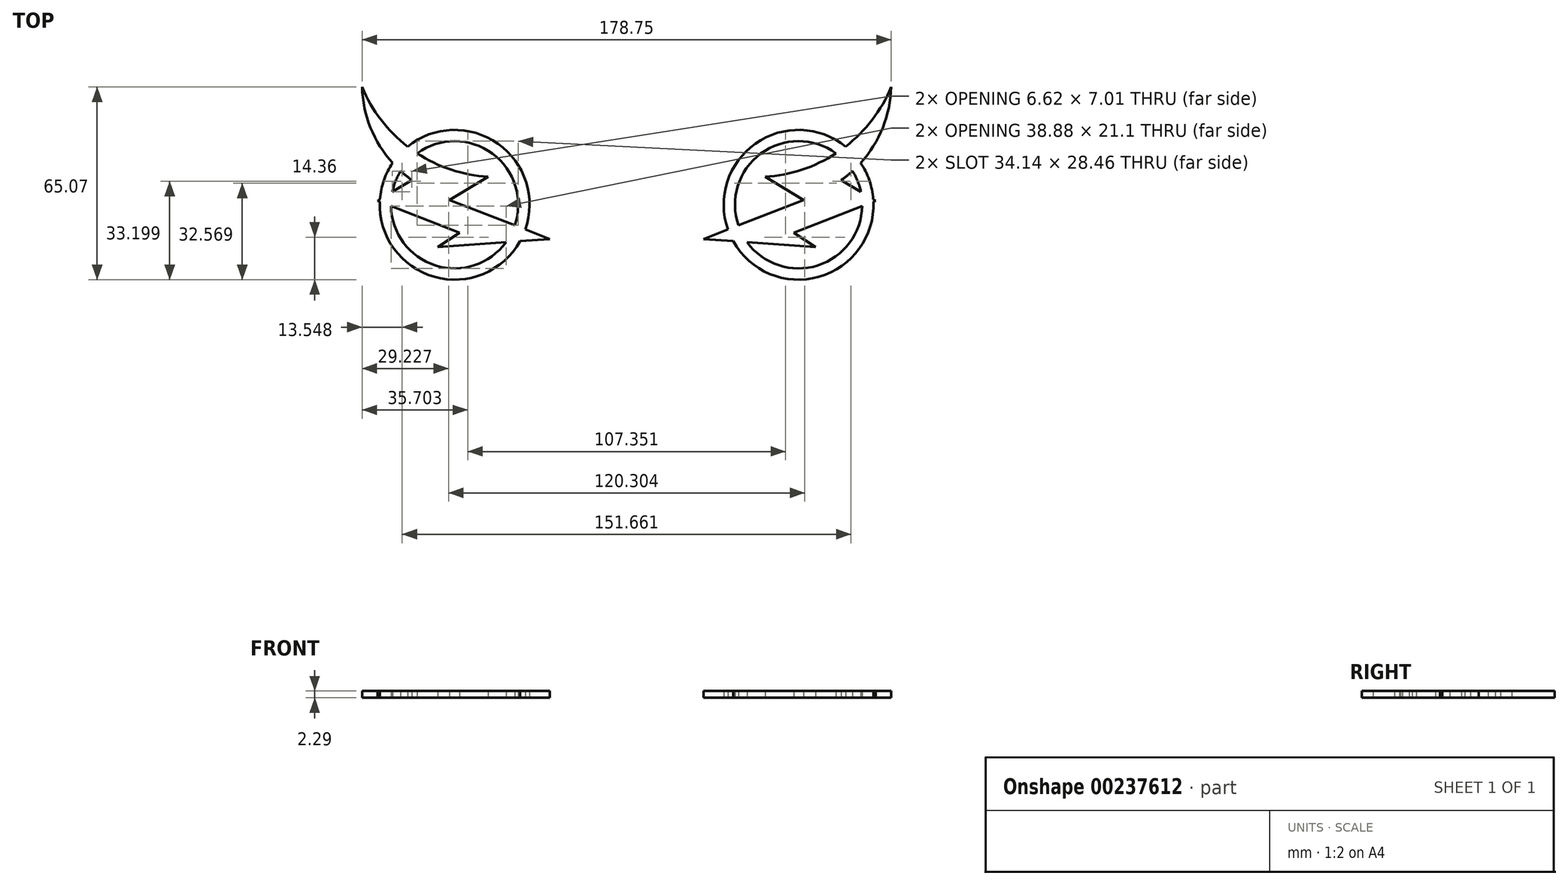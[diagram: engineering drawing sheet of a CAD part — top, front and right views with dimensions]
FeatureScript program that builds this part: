
annotation { "Feature Type Name" : "Feature", "Feature Type Description" : "" }
export const myFeature = defineFeature(function(context is Context, id is Id, definition is map)
    precondition{}
    {
        {
            var Q0;
            Q0=qCreatedBy(makeId("Top.planeOp"),FACE);
            var sketch = newSketch(context, id + "F0", { "sketchPlane" : qUnion([Q0])});
            skArc(sketch, "E0", {"start": v(-29.54, 23.2) * mm, "mid": v(-23.15, 12.16) * mm, "end": v(-14.15, 3.13) * mm});
            skLineSegment(sketch, "E1", {"start": v(13.05, -7.14) * mm, "end": v(0, -14.95) * mm});
            skLineSegment(sketch, "E2", {"start": v(0, -14.95) * mm, "end": v(22.07, -23.53) * mm});
            skLineSegment(sketch, "E3", {"start": v(33.89, -28.13) * mm, "end": v(23.86, -28.86) * mm});
            skLineSegment(sketch, "E4", {"start": v(-3.95, -30.88) * mm, "end": v(3.39, -25.96) * mm});
            skLineSegment(sketch, "E5", {"start": v(3.39, -25.96) * mm, "end": v(-19.75, -16.96) * mm});
            skLineSegment(sketch, "E6", {"start": v(-24.33, -15.18) * mm, "end": v(-23.5, -14.69) * mm});
            skArc(sketch, "E7", {"start": v(-29.54, 23.2) * mm, "mid": v(-26.67, 9.47) * mm, "end": v(-19.24, -2.41) * mm});
            skArc(sketch, "E8", {"start": v(-16.48, -5.17) * mm, "mid": v(-18.2, -8.55) * mm, "end": v(-19.3, -12.18) * mm});
            skArc(sketch, "E9.0", {"start": v(-19.24, -2.41) * mm, "mid": v(-22.17, -8.27) * mm, "end": v(-23.5, -14.69) * mm});
            skArc(sketch, "E10.trimOffspring", {"start": v(-10.9, 0.82) * mm, "mid": v(0.56, -4.71) * mm, "end": v(13.05, -7.14) * mm});
            skArc(sketch, "E11.trimOffspring", {"start": v(-16.48, -5.17) * mm, "mid": v(-14.63, -6.75) * mm, "end": v(-12.68, -8.21) * mm});
            skLineSegment(sketch, "E12.trimOffspring", {"start": v(-23.54, -15.49) * mm, "end": v(-24.33, -15.18) * mm});
            skLineSegment(sketch, "E13.trimOffspring", {"start": v(-19.3, -12.18) * mm, "end": v(-12.68, -8.21) * mm});
            skArc(sketch, "E14.trimOffspring", {"start": v(-19.75, -16.96) * mm, "mid": v(-4.72, -37.07) * mm, "end": v(19.12, -29.2) * mm});
            skArc(sketch, "E15.trimOffspring", {"start": v(-23.54, -15.49) * mm, "mid": v(-5.13, -40.92) * mm, "end": v(23.86, -28.86) * mm});
            skLineSegment(sketch, "E16.trimOffspring", {"start": v(19.12, -29.2) * mm, "end": v(-3.95, -30.88) * mm});
            skLineSegment(sketch, "E17.trimOffspring", {"start": v(25.63, -24.91) * mm, "end": v(33.89, -28.13) * mm});
            skArc(sketch, "E18.trimOffspring", {"start": v(22.07, -23.53) * mm, "mid": v(14.5, 0.73) * mm, "end": v(-10.9, 0.82) * mm});
            skArc(sketch, "E19.trimOffspring", {"start": v(25.63, -24.91) * mm, "mid": v(16.32, 4.12) * mm, "end": v(-14.15, 3.13) * mm});
            skArc(sketch, "E20.MirrorCS", {"start": v(97.6, -23.53) * mm, "mid": v(105.17, 0.73) * mm, "end": v(130.58, 0.82) * mm});
            skArc(sketch, "E21.MirrorCS", {"start": v(94.05, -24.91) * mm, "mid": v(103.36, 4.12) * mm, "end": v(133.83, 3.13) * mm});
            skArc(sketch, "E22.MirrorCS", {"start": v(130.58, 0.82) * mm, "mid": v(119.12, -4.71) * mm, "end": v(106.62, -7.14) * mm});
            skLineSegment(sketch, "E23.MirrorCS", {"start": v(119.68, -14.95) * mm, "end": v(97.6, -23.53) * mm});
            skLineSegment(sketch, "E24.MirrorCS", {"start": v(94.05, -24.91) * mm, "end": v(85.79, -28.13) * mm});
            skLineSegment(sketch, "E25.MirrorCS", {"start": v(85.79, -28.13) * mm, "end": v(95.82, -28.86) * mm});
            skArc(sketch, "E26.MirrorCS", {"start": v(139.43, -16.96) * mm, "mid": v(124.4, -37.07) * mm, "end": v(100.55, -29.2) * mm});
            skArc(sketch, "E27.MirrorCS", {"start": v(143.22, -15.49) * mm, "mid": v(124.8, -40.92) * mm, "end": v(95.82, -28.86) * mm});
            skLineSegment(sketch, "E28.MirrorCS", {"start": v(100.55, -29.2) * mm, "end": v(123.63, -30.88) * mm});
            skLineSegment(sketch, "E29.MirrorCS", {"start": v(123.63, -30.88) * mm, "end": v(116.3, -25.96) * mm});
            skLineSegment(sketch, "E30.MirrorCS", {"start": v(116.3, -25.96) * mm, "end": v(139.43, -16.96) * mm});
            skLineSegment(sketch, "E31.MirrorCS", {"start": v(138.98, -12.18) * mm, "end": v(132.36, -8.21) * mm});
            skArc(sketch, "E32.MirrorCS", {"start": v(136.16, -5.17) * mm, "mid": v(137.88, -8.55) * mm, "end": v(138.98, -12.18) * mm});
            skArc(sketch, "E33.MirrorCS", {"start": v(136.16, -5.17) * mm, "mid": v(134.3, -6.75) * mm, "end": v(132.36, -8.21) * mm});
            skArc(sketch, "E34.MirrorCS", {"start": v(149.21, 23.2) * mm, "mid": v(142.82, 12.16) * mm, "end": v(133.83, 3.13) * mm});
            skArc(sketch, "E35.MirrorCS", {"start": v(149.21, 23.2) * mm, "mid": v(146.35, 9.47) * mm, "end": v(138.91, -2.41) * mm});
            skArc(sketch, "E36.MirrorCS", {"start": v(138.91, -2.41) * mm, "mid": v(141.84, -8.27) * mm, "end": v(143.17, -14.69) * mm});
            skLineSegment(sketch, "E37.MirrorCS", {"start": v(106.62, -7.14) * mm, "end": v(119.68, -14.95) * mm});
            skLineSegment(sketch, "E38.MirrorCS", {"start": v(143.22, -15.49) * mm, "end": v(144, -15.18) * mm});
            skLineSegment(sketch, "E39.MirrorCS", {"start": v(144, -15.18) * mm, "end": v(143.17, -14.69) * mm});
            skSolve(sketch);
        }
        {
            var Q0;
            Q0 = qSketchRegion(id + "F0", true);
            extrude(context, id + "F1", {"entities" : qUnion([Q0]), "depth" : 2.3 * mm});
        }
    });
